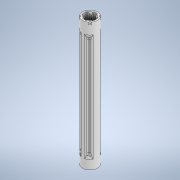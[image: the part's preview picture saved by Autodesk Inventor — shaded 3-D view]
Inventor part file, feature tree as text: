
AUTODESK INVENTOR PART (.ipt)
format: ipt  version: 2022 (Build 260153000, 153)  size: 486,400 bytes
history: native  units: in
note: dims shown in document units (in); Inventor stores cm internally (conversion verified against a paired STEP export)
features: sketch x7, extrude x6, fillet x2, mirror x2, chamfer x1, plane x1, revolve x1
ambient origin geometry x8: Origin, YZ Plane, XZ Plane, XY Plane, X Axis, Y Axis, Z Axis, Center Point
bodies: Solid1 (feature_tree)
feature tree (20):
  extrude  "Extrusion1"  Depth=5.0394in TaperAngle=0.0deg
  extrude  "Extrusion2"  Depth=0.7087in
  extrude  "Extrusion3"  Depth=0.315in TaperAngle=0.0deg
  extrude  "Extrusion6"  Depth=0.0394in
  extrude  "Extrusion7"  Depth=0.0394in
  extrude  "Extrusion14"  Depth=0.1949in
  chamfer  "Chamfer1"  Distance=1.5748in Angle=360.0deg
  plane  "Work Plane1"
  revolve  "Revolution1"  [1 undecoded]
  fillet  "Fillet3"  Radius=0.3898in
  fillet  "Fillet4"  Radius=0.2126in
  mirror  "Mirror1"
  mirror  "Mirror2"
  sketch  "Sketch1"  dims[d0=0.5512in d1=5.0394in d2=0.0in]
  sketch  "Sketch2"  dims[d13=0.0in d14=0.0in d15=0.7087in]
  sketch  "Sketch3"  dims[d19=0.3543in d20=0.315in d21=0.0in]
  sketch  "Sketch6"  dims[d36=0.0394in d37=0.0394in]
  sketch  "Sketch7"  dims[d38=0.0394in d39=0.0394in]
  sketch  "Sketch12"  dims[d69=0.0787in d70=0.1949in]
  sketch  "Sketch13"  dims[d71=0.1949in d72=1.5748in d74=360.0deg d76=0.0787in d77=0.0in d78=0.3898in d79=0.2126in d80=0.0in d81=0.0in d93=0.3071in d94=0.1339in d95=0.122in d97=1.5748in d99=360.0deg d120=0.1535in d121=0.122in d128=0.7874in d129=0.0in d130=0.0394in d131=0.0787in d132=60.0deg d133=45.0deg d134=3.8583in d135=0.0591in d136=0.3937in d137=0.1374in d138=0.0344in d139=0.1575in d140=0.0472in d67=0.0197in d68=0.0344in d91=0.0197in d92=0.0344in d109=0.0197in d110=0.0344in d111=0.0197in d112=0.0344in]
note: 1 required parameter value undecoded (feature->parameter linkage not recoverable at this tier; creation-order binding heuristic only, values carry confidence <= 0.55)
